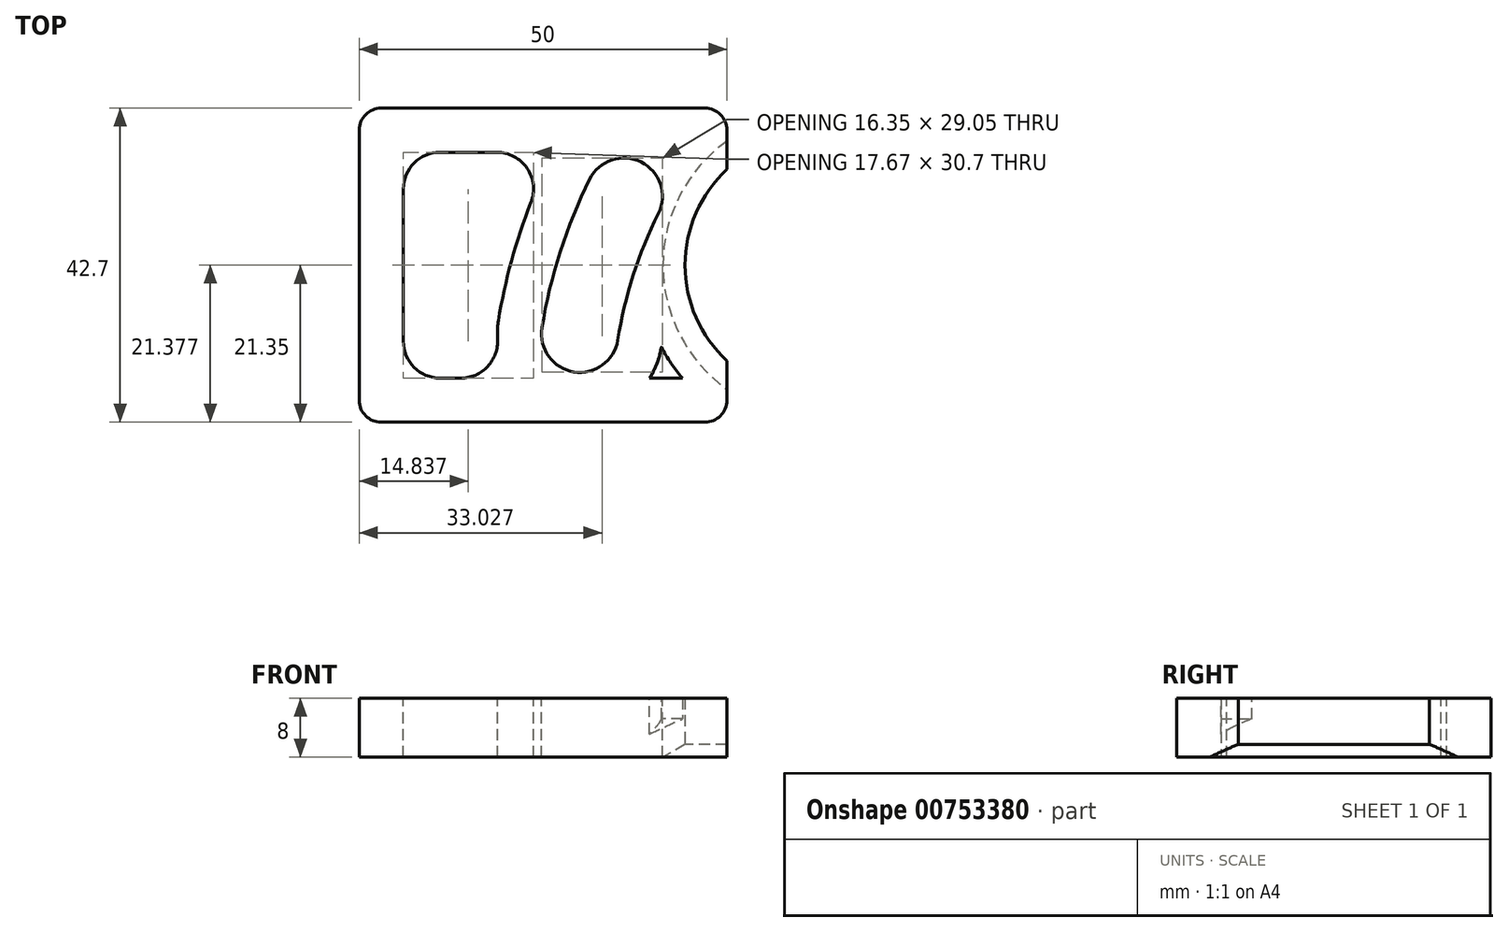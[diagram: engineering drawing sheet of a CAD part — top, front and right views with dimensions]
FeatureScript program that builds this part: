
annotation { "Feature Type Name" : "Feature", "Feature Type Description" : "" }
export const myFeature = defineFeature(function(context is Context, id is Id, definition is map)
    precondition{}
    {
        {
            var Q0;
            Q0=qCreatedBy(makeId("Top.planeOp"),FACE);
            var sketch = newSketch(context, id + "F0", { "sketchPlane" : qUnion([Q0])});
            skLineSegment(sketch, "E0.bottom", {"start": v(-25, 21.35) * mm, "end": v(25, 21.35) * mm});
            skLineSegment(sketch, "E0.top", {"start": v(-25, -21.35) * mm, "end": v(25, -21.35) * mm});
            skLineSegment(sketch, "E0.left", {"start": v(-25, 21.35) * mm, "end": v(-25, -21.35) * mm});
            skLineSegment(sketch, "E0.right", {"start": v(25, 21.35) * mm, "end": v(25, 13.01) * mm});
            skLineSegment(sketch, "E1", {"start": v(-25, 21.35) * mm, "end": v(25, -21.35) * mm, "construction": true});
            skArc(sketch, "E2", {"start": v(25, 13.01) * mm, "mid": v(19.3, 0) * mm, "end": v(25, -13.01) * mm});
            skLineSegment(sketch, "E3.trimOffspring", {"start": v(25, -13.01) * mm, "end": v(25, -21.35) * mm});
            skCircle(sketch, "E4", {"center": v(37, 0) * mm, "radius": 17.7 * mm, "construction": true});
            skSolve(sketch);
        }
        {
            var Q0;
            Q0=qSketchRegion(id+"F0",true);
            extrude(context, id + "F1", {"entities" : qUnion([Q0]), "depth" : 8 * mm});
        }
        {
            var Q0;
            Q0=makeQuery(id+"F1.opExtrude","CAP_EDGE",EDGE,{"disambiguationData":[OSD([sQuery(id+"F0.wireOp",EDGE,"E2")])],"isStart":true});
            chamfer(context, id + "F2", {"entities" : qUnion([Q0]), "chamferType" : ChamferType.OFFSET_ANGLE, "width" : 3 * mm, "oppositeDirection" : false, "angle" : 30 * degree, "tangentPropagation" : true});
        }
        {
            var Q0;
            Q0=makeQuery(id+"F1.opExtrude","CAP_FACE",FACE,{"disambiguationData":[OSD([sQuery(id+"F0.wireOp",EDGE,"E0.bottom"),sQuery(id+"F0.wireOp",EDGE,"E0.top"),sQuery(id+"F0.wireOp",EDGE,"E0.left"),sQuery(id+"F0.wireOp",EDGE,"E0.right"),sQuery(id+"F0.wireOp",EDGE,"E2"),sQuery(id+"F0.wireOp",EDGE,"E3.trimOffspring")])],"isStart":false});
            var sketch = newSketch(context, id + "F3", { "sketchPlane" : qUnion([Q0])});
            skArc(sketch, "E5", {"start": v(6.33, 11.67) * mm, "mid": v(2.33, 1.82) * mm, "end": v(-0.15, -8.52) * mm});
            skArc(sketch, "E6", {"start": v(15.67, 7.03) * mm, "mid": v(12.26, -1.37) * mm, "end": v(10.15, -10.18) * mm});
            skArc(sketch, "E7", {"start": v(6.33, 11.67) * mm, "mid": v(13.32, 14.02) * mm, "end": v(15.67, 7.03) * mm});
            skArc(sketch, "E8", {"start": v(-0.15, -8.52) * mm, "mid": v(4.17, -14.5) * mm, "end": v(10.15, -10.18) * mm});
            skSolve(sketch);
        }
        {
            var Q0;
            Q0=qSketchRegion(id+"F3",true);
            extrude(context, id + "F4", {"entities" : qUnion([Q0]), "operationType" : NewBodyOperationType.REMOVE, "endBound" : BoundingType.THROUGH_ALL, "oppositeDirection" : true, "depth" : 25 * mm});
        }
        {
            var Q0;
            Q0=makeQuery(id+"F1.opExtrude","SWEPT_EDGE",EDGE,{"disambiguationData":[OSD([sQuery(id+"F0.wireOp",EDGE,"E0.top"),sQuery(id+"F0.wireOp",EDGE,"E0.left")])]});
            var Q1;
            Q1=makeQuery(id+"F1.opExtrude","SWEPT_EDGE",EDGE,{"disambiguationData":[OSD([sQuery(id+"F0.wireOp",EDGE,"E0.top"),sQuery(id+"F0.wireOp",EDGE,"E3.trimOffspring")])]});
            var Q2;
            Q2=makeQuery(id+"F1.opExtrude","SWEPT_EDGE",EDGE,{"disambiguationData":[OSD([sQuery(id+"F0.wireOp",EDGE,"E0.bottom"),sQuery(id+"F0.wireOp",EDGE,"E0.right")])]});
            var Q3;
            Q3=makeQuery(id+"F1.opExtrude","SWEPT_EDGE",EDGE,{"disambiguationData":[OSD([sQuery(id+"F0.wireOp",EDGE,"E0.bottom"),sQuery(id+"F0.wireOp",EDGE,"E0.left")])]});
            fillet(context, id + "F5", {"entities" : qUnion([Q0, Q1, Q2, Q3]), "radius" : 3 * mm, "tangentPropagation" : true, "allowEdgeOverflow" : false});
        }
        {
            var Q0;
            Q0=makeQuery(id+"F1.opExtrude","CAP_FACE",FACE,{"disambiguationData":[OSD([sQuery(id+"F0.wireOp",EDGE,"E0.bottom"),sQuery(id+"F0.wireOp",EDGE,"E0.top"),sQuery(id+"F0.wireOp",EDGE,"E0.left"),sQuery(id+"F0.wireOp",EDGE,"E0.right"),sQuery(id+"F0.wireOp",EDGE,"E2"),sQuery(id+"F0.wireOp",EDGE,"E3.trimOffspring")])],"isStart":false});
            var Q1;
            Q1=makeQuery(id+"F1.opExtrude","CAP_FACE",FACE,{"disambiguationData":[OSD([sQuery(id+"F0.wireOp",EDGE,"E0.bottom"),sQuery(id+"F0.wireOp",EDGE,"E0.top"),sQuery(id+"F0.wireOp",EDGE,"E0.left"),sQuery(id+"F0.wireOp",EDGE,"E0.right"),sQuery(id+"F0.wireOp",EDGE,"E2"),sQuery(id+"F0.wireOp",EDGE,"E3.trimOffspring")])],"isStart":true});
            shell(context, id + "F6", {"entities" : qUnion([Q0, Q1]), "thickness" : 6 * mm});
        }
        {
            var Q0;
            Q0=makeQuery(id+"F6.opShell","OFFSET_EDGE",EDGE,{"disambiguationData":[OSD([sQuery(id+"F0.wireOp",EDGE,"E0.bottom"),sQuery(id+"F0.wireOp",EDGE,"E0.left")])]});
            var Q1;
            Q1=makeQuery(id+"F6.opShell","TWEAK_EDGE",EDGE,{"disambiguationData":[OD(1.0)],"derivedFrom":[makeQuery(id+"F4.boolean.opBoolean","COPY",FACE,{"derivedFrom":makeQuery(id+"F4.opExtrude","SWEPT_FACE",FACE,{"disambiguationData":[OSD([sQuery(id+"F3.wireOp",EDGE,"E7")])]})}),makeQuery(id+"F1.opExtrude","SWEPT_FACE",FACE,{"disambiguationData":[OSD([sQuery(id+"F0.wireOp",EDGE,"E0.bottom")])]})]});
            var Q2;
            Q2=makeQuery(id+"F6.opShell","OFFSET_EDGE",EDGE,{"disambiguationData":[OSD([sQuery(id+"F0.wireOp",EDGE,"E0.top"),sQuery(id+"F0.wireOp",EDGE,"E0.left")])]});
            var Q3;
            Q3=makeQuery(id+"F6.opShell","TWEAK_EDGE",EDGE,{"disambiguationData":[OD(1.0)],"derivedFrom":[makeQuery(id+"F4.boolean.opBoolean","COPY",FACE,{"derivedFrom":makeQuery(id+"F4.opExtrude","SWEPT_FACE",FACE,{"disambiguationData":[OSD([sQuery(id+"F3.wireOp",EDGE,"E8")])]})}),makeQuery(id+"F1.opExtrude","SWEPT_FACE",FACE,{"disambiguationData":[OSD([sQuery(id+"F0.wireOp",EDGE,"E0.top")])]})]});
            fillet(context, id + "F7", {"entities" : qUnion([Q0, Q1, Q2, Q3]), "radius" : 5 * mm, "tangentPropagation" : true, "allowEdgeOverflow" : false});
        }
    });
